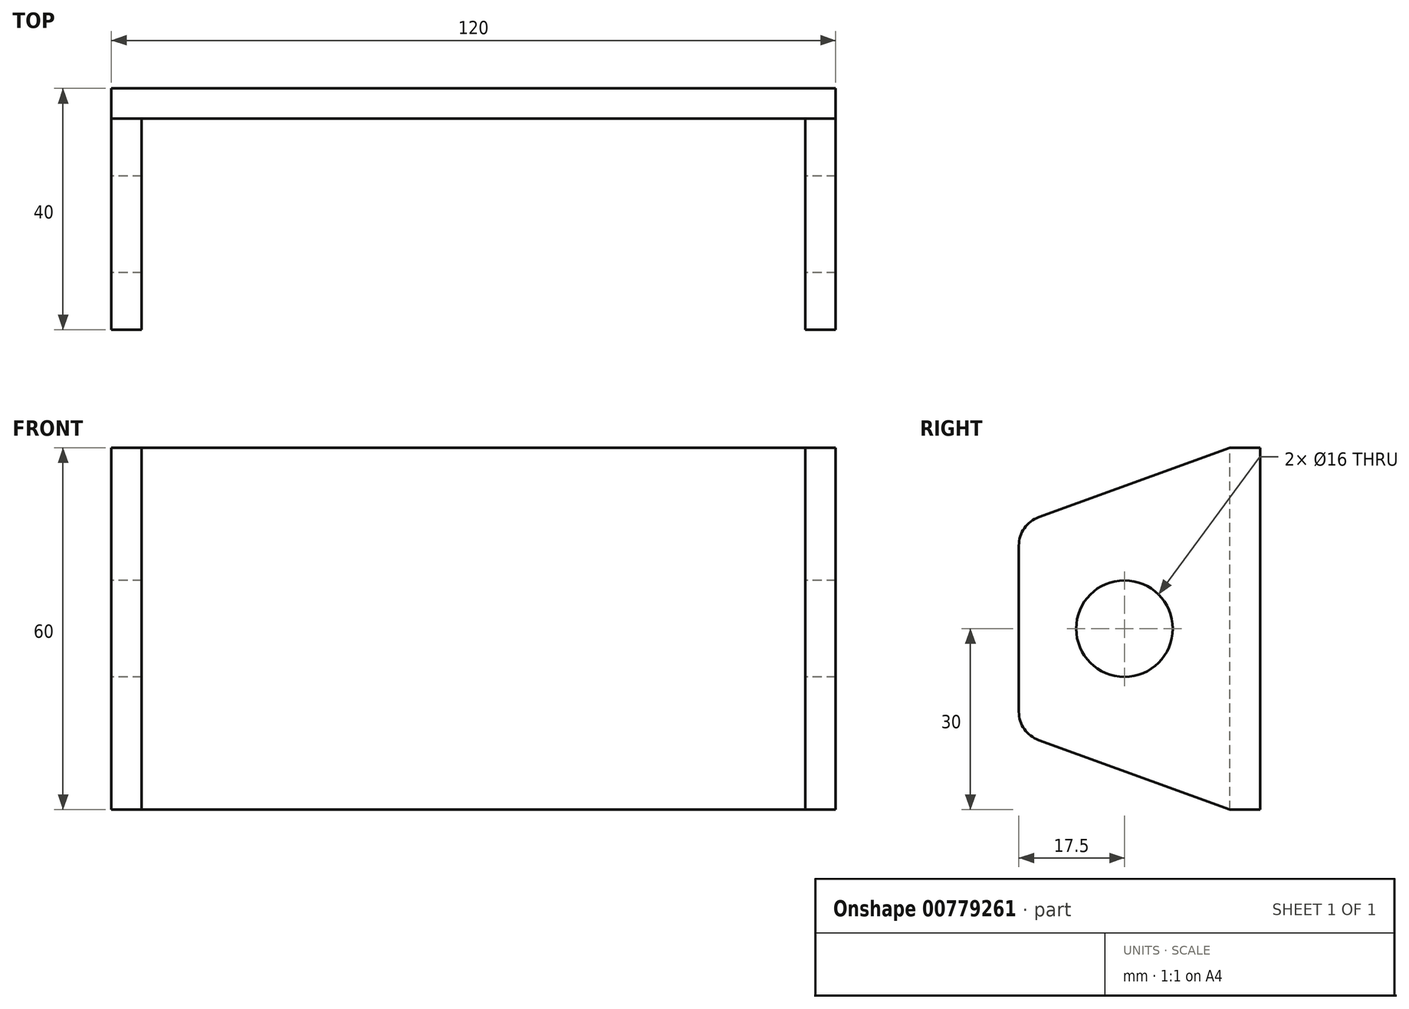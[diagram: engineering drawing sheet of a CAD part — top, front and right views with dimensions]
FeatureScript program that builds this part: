
annotation { "Feature Type Name" : "Feature", "Feature Type Description" : "" }
export const myFeature = defineFeature(function(context is Context, id is Id, definition is map)
    precondition{}
    {
        {
            var Q0;
            Q0=qCreatedBy(makeId("Front.planeOp"),FACE);
            var sketch = newSketch(context, id + "F0", { "sketchPlane" : qUnion([Q0])});
            skLineSegment(sketch, "E0.bottom", {"start": v(0, 0) * mm, "end": v(120, 0) * mm});
            skLineSegment(sketch, "E0.top", {"start": v(0, 60) * mm, "end": v(120, 60) * mm});
            skLineSegment(sketch, "E0.left", {"start": v(0, 0) * mm, "end": v(0, 60) * mm});
            skLineSegment(sketch, "E0.right", {"start": v(120, 0) * mm, "end": v(120, 60) * mm});
            skSolve(sketch);
        }
        {
            var Q0;
            Q0=qSketchRegion(id+"F0",true);
            extrude(context, id + "F1", {"entities" : qUnion([Q0]), "depth" : 5 * mm});
        }
        {
            var Q0;
            Q0=makeQuery(id+"F1.opExtrude","SWEPT_FACE",FACE,{"disambiguationData":[OSD([sQuery(id+"F0.wireOp",EDGE,"E0.left")])]});
            var sketch = newSketch(context, id + "F2", { "sketchPlane" : qUnion([Q0])});
            skLineSegment(sketch, "E1", {"start": v(5, 60) * mm, "end": v(40, 47.26) * mm});
            skLineSegment(sketch, "E2", {"start": v(40, 47.26) * mm, "end": v(40, 12.74) * mm});
            skLineSegment(sketch, "E3", {"start": v(40, 12.74) * mm, "end": v(5, 0) * mm});
            skSolve(sketch);
        }
        {
            var Q0;
            Q0=makeQuery(id+"F2.imprint","IMPRINT",FACE,{"disambiguationData":[TD([[makeQuery(id+"F2.imprint","IMPRINT",EDGE,{"derivedFrom":sQuery(id+"F2.wireOp",EDGE,"E1")}),-1.0]])]});
            extrude(context, id + "F3", {"entities" : qUnion([Q0]), "operationType" : NewBodyOperationType.ADD, "oppositeDirection" : true, "depth" : 5 * mm});
        }
        {
            var Q0;
            {var subQ0=sQuery(id+"F0.wireOp",EDGE,"E0.left");Q0=makeQuery(id+"F3.boolean.opBoolean","MERGE",FACE,{"derivedFrom":[makeQuery(id+"F1.opExtrude","SWEPT_FACE",FACE,{"disambiguationData":[OSD([subQ0])]}),makeQuery(id+"F3.opExtrude","CAP_FACE",FACE,{"disambiguationData":[OSD([subQ0,sQuery(id+"F2.wireOp",EDGE,"E1"),sQuery(id+"F2.wireOp",EDGE,"E2"),sQuery(id+"F2.wireOp",EDGE,"E3")])],"isStart":true})]});}
            var sketch = newSketch(context, id + "F4", { "sketchPlane" : qUnion([Q0])});
            skCircle(sketch, "E4", {"center": v(22.5, 30) * mm, "radius": 8 * mm});
            skSolve(sketch);
        }
        {
            var Q0;
            Q0=makeQuery(id+"F1.opExtrude","SWEPT_FACE",FACE,{"disambiguationData":[OSD([sQuery(id+"F0.wireOp",EDGE,"E0.right")])]});
            var sketch = newSketch(context, id + "F5", { "sketchPlane" : qUnion([Q0])});
            skLineSegment(sketch, "E5", {"start": v(-5, 60) * mm, "end": v(-40, 47.26) * mm});
            skLineSegment(sketch, "E6", {"start": v(-40, 47.26) * mm, "end": v(-40, 12.74) * mm});
            skLineSegment(sketch, "E7", {"start": v(-40, 12.74) * mm, "end": v(-5, 0) * mm});
            skSolve(sketch);
        }
        {
            var Q0;
            Q0=makeQuery(id+"F5.imprint","IMPRINT",FACE,{"disambiguationData":[TD([[makeQuery(id+"F5.imprint","IMPRINT",EDGE,{"derivedFrom":sQuery(id+"F5.wireOp",EDGE,"E5")}),1.0]])]});
            extrude(context, id + "F6", {"entities" : qUnion([Q0]), "operationType" : NewBodyOperationType.ADD, "oppositeDirection" : true, "depth" : 5 * mm});
        }
        {
            var Q0;
            Q0=makeQuery(id+"F4.imprint","IMPRINT",FACE,{"disambiguationData":[TD([[makeQuery(id+"F4.imprint","IMPRINT",EDGE,{"derivedFrom":sQuery(id+"F4.wireOp",EDGE,"E4")}),1.0]])]});
            extrude(context, id + "F7", {"entities" : qUnion([Q0]), "operationType" : NewBodyOperationType.REMOVE, "oppositeDirection" : true, "depth" : 146 * mm});
        }
        {
            var Q0;
            Q0=makeQuery(id+"F3.opExtrude","SWEPT_EDGE",EDGE,{"disambiguationData":[OSD([sQuery(id+"F2.wireOp",EDGE,"E1"),sQuery(id+"F2.wireOp",EDGE,"E2")])]});
            var Q1;
            Q1=makeQuery(id+"F3.opExtrude","SWEPT_EDGE",EDGE,{"disambiguationData":[OSD([sQuery(id+"F2.wireOp",EDGE,"E2"),sQuery(id+"F2.wireOp",EDGE,"E3")])]});
            var Q2;
            Q2=makeQuery(id+"F6.opExtrude","SWEPT_EDGE",EDGE,{"disambiguationData":[OSD([sQuery(id+"F5.wireOp",EDGE,"E5"),sQuery(id+"F5.wireOp",EDGE,"E6")])]});
            var Q3;
            Q3=makeQuery(id+"F6.opExtrude","SWEPT_EDGE",EDGE,{"disambiguationData":[OSD([sQuery(id+"F5.wireOp",EDGE,"E6"),sQuery(id+"F5.wireOp",EDGE,"E7")])]});
            fillet(context, id + "F8", {"entities" : qUnion([Q0, Q1, Q2, Q3]), "radius" : 5 * mm, "tangentPropagation" : true, "allowEdgeOverflow" : false});
        }
    });
